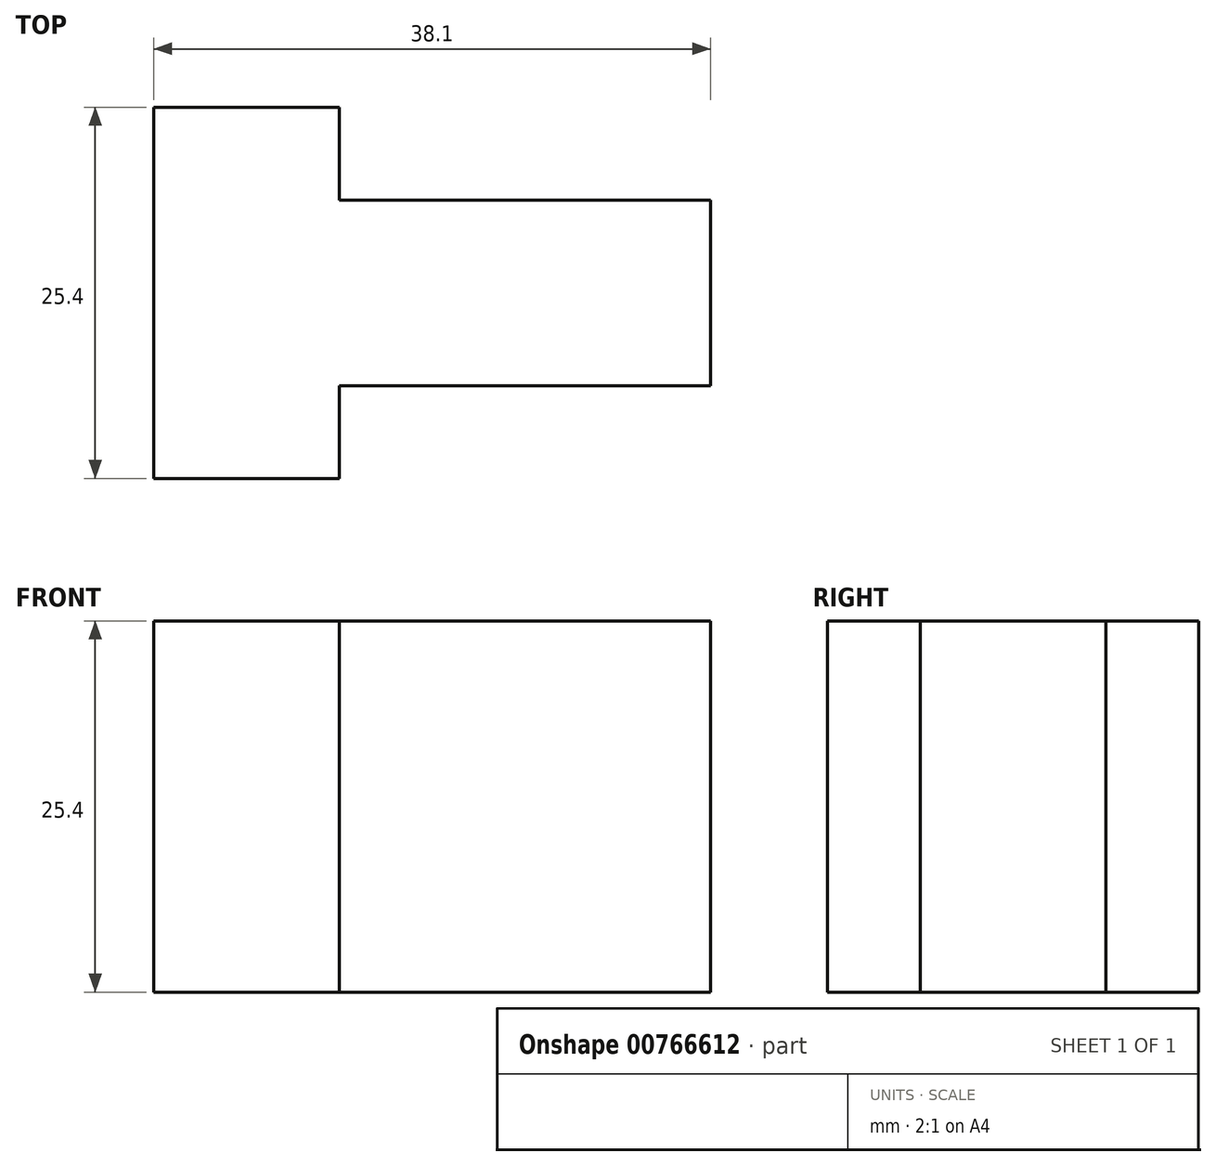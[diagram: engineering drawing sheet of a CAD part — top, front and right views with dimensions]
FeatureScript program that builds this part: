
annotation { "Feature Type Name" : "Feature", "Feature Type Description" : "" }
export const myFeature = defineFeature(function(context is Context, id is Id, definition is map)
    precondition{}
    {
        {
            var Q0;
            Q0=qCreatedBy(makeId("Top.planeOp"),FACE);
            var sketch = newSketch(context, id + "F0", { "sketchPlane" : qUnion([Q0])});
            skLineSegment(sketch, "E0", {"start": v(0, 0) * mm, "end": v(0, 25.4) * mm});
            skLineSegment(sketch, "E1", {"start": v(0, 25.4) * mm, "end": v(12.7, 25.4) * mm});
            skLineSegment(sketch, "E2", {"start": v(12.7, 25.4) * mm, "end": v(12.7, 19.05) * mm});
            skLineSegment(sketch, "E3", {"start": v(12.7, 19.05) * mm, "end": v(38.1, 19.05) * mm});
            skLineSegment(sketch, "E4", {"start": v(38.1, 19.05) * mm, "end": v(38.1, 6.35) * mm});
            skLineSegment(sketch, "E5", {"start": v(38.1, 6.35) * mm, "end": v(12.7, 6.35) * mm});
            skLineSegment(sketch, "E6", {"start": v(12.7, 6.35) * mm, "end": v(12.7, 0) * mm});
            skLineSegment(sketch, "E7", {"start": v(12.7, 0) * mm, "end": v(0, 0) * mm});
            skSolve(sketch);
        }
        {
            var Q0;
            Q0 = qSketchRegion(id + "F0", true);
            extrude(context, id + "F1", {"entities" : qUnion([Q0]), "depth" : 25.4 * mm, "offsetDistance" : 25.4 * mm});
        }
    });
